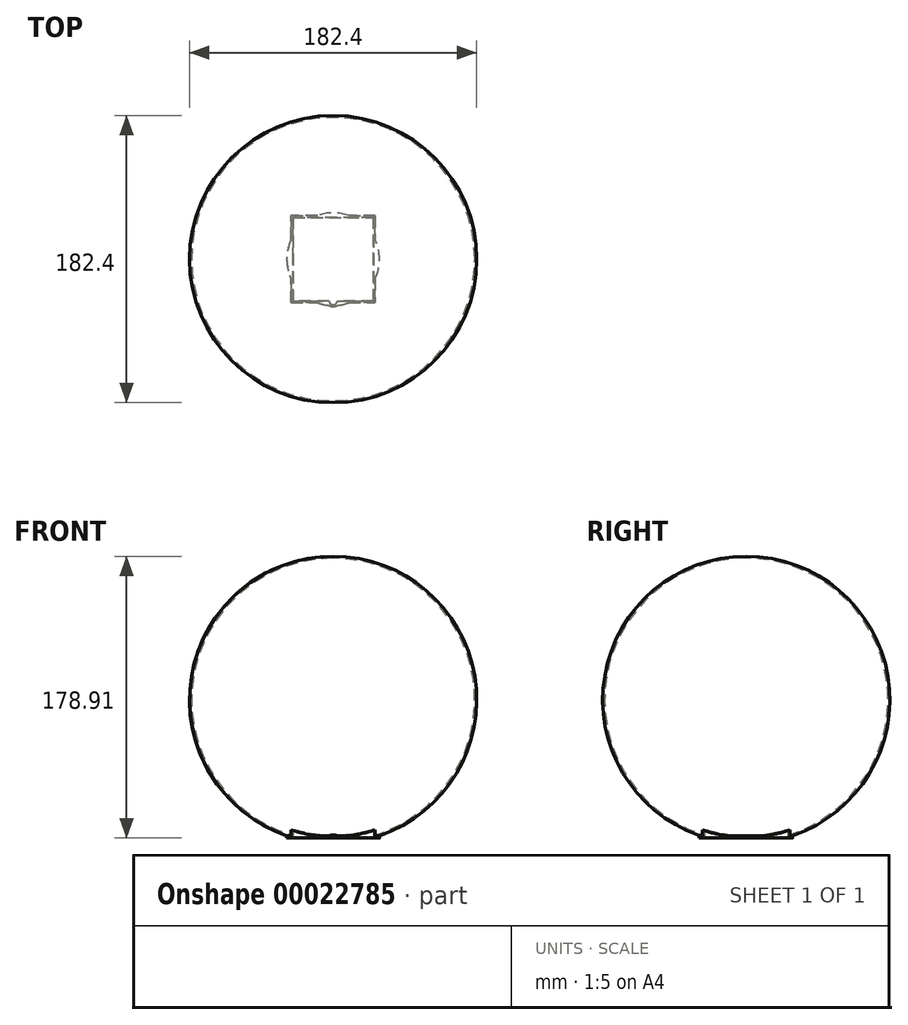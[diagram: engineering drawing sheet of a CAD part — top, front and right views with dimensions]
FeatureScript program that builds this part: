
annotation { "Feature Type Name" : "Feature", "Feature Type Description" : "" }
export const myFeature = defineFeature(function(context is Context, id is Id, definition is map)
    precondition{}
    {
        {
            var Q0;
            Q0=qCreatedBy(makeId("Top.planeOp"),FACE);
            var sketch = newSketch(context, id + "F0", { "sketchPlane" : qUnion([Q0])});
            skLineSegment(sketch, "E0.bottom", {"start": v(-25.5, 26.5) * mm, "end": v(25.5, 26.5) * mm});
            skLineSegment(sketch, "E0.top", {"start": v(-25.5, -26.5) * mm, "end": v(-2.5, -26.5) * mm});
            skLineSegment(sketch, "E0.left", {"start": v(-25.5, 26.5) * mm, "end": v(-25.5, -26.5) * mm});
            skLineSegment(sketch, "E0.right", {"start": v(25.5, 26.5) * mm, "end": v(25.5, -26.5) * mm});
            skPoint(sketch, "E0.middle", {"position": v(0, 0) * mm});
            skArc(sketch, "E1", {"start": v(-2.5, -26.5) * mm, "mid": v(0, -29) * mm, "end": v(2.5, -26.5) * mm});
            skLineSegment(sketch, "E2.trimOffspring", {"start": v(2.5, -26.5) * mm, "end": v(25.5, -26.5) * mm});
            skSolve(sketch);
        }
        {
            var Q0;
            Q0=makeQuery(id+"F0.imprint","IMPRINT",FACE,{"disambiguationData":[TD([[makeQuery(id+"F0.imprint","IMPRINT",EDGE,{"derivedFrom":sQuery(id+"F0.wireOp",EDGE,"E0.bottom")}),-1.0]])]});
            extrude(context, id + "F1", {"entities" : qUnion([Q0]), "depth" : 3 * mm});
        }
        {
            var Q0;
            Q0=qCreatedBy(makeId("Front.planeOp"),FACE);
            var sketch = newSketch(context, id + "F2", { "sketchPlane" : qUnion([Q0])});
            skLineSegment(sketch, "E3", {"start": v(0, 0) * mm, "end": v(0, 176.31) * mm});
            skLineSegment(sketch, "E4.0", {"start": v(-25.5, 0) * mm, "end": v(-2.5, 0) * mm});
            skLineSegment(sketch, "E4.1", {"start": v(-2.5, 0) * mm, "end": v(2.5, 0) * mm});
            skLineSegment(sketch, "E4.2", {"start": v(2.5, 0) * mm, "end": v(25.5, 0) * mm});
            skArc(sketch, "E5", {"start": v(-25.5, 0) * mm, "mid": v(0, 176.31) * mm, "end": v(25.5, 0) * mm});
            skSolve(sketch);
        }
        {
            var Q0;
            {var subQ3=sQuery(id+"F2.wireOp",EDGE,"E3");Q0=makeQuery(id+"F2.imprint","IMPRINT",FACE,{"disambiguationData":[TD([[makeQuery(id+"F2.imprint","IMPRINT",EDGE,{"derivedFrom":subQ3}),1.0]])]});}
            var Q1;
            Q1=sQuery(id+"F2.wireOp",EDGE,"E3");
            revolve(context, id + "F3", {"operationType" : NewBodyOperationType.ADD, "entities" : qUnion([Q0]), "axis" : qUnion([Q1]), "revolveType" : RevolveType.FULL});
        }
        {
            var Q0;
            Q0=makeQuery(id+"F1.opExtrude","CAP_FACE",FACE,{"disambiguationData":[OSD([sQuery(id+"F0.wireOp",EDGE,"E0.bottom"),sQuery(id+"F0.wireOp",EDGE,"E0.top"),sQuery(id+"F0.wireOp",EDGE,"E0.left"),sQuery(id+"F0.wireOp",EDGE,"E0.right")])],"isStart":true});
            shell(context, id + "F4", {"entities" : qUnion([Q0]), "thickness" : 1.2 * mm, "oppositeDirection" : true});
        }
        {
            var Q0;
            Q0=makeQuery(id+"F1.opExtrude","CAP_FACE",FACE,{"disambiguationData":[OSD([sQuery(id+"F0.wireOp",EDGE,"E0.bottom"),sQuery(id+"F0.wireOp",EDGE,"E0.top"),sQuery(id+"F0.wireOp",EDGE,"E0.left"),sQuery(id+"F0.wireOp",EDGE,"E0.right")])],"isStart":true});
            extrude(context, id + "F5", {"entities" : qUnion([Q0]), "operationType" : NewBodyOperationType.ADD, "depth" : 1.4 * mm});
        }
        {
            var Q0;
            {var subQ0=sQuery(id+"F2.wireOp",EDGE,"E5");var subQ1=sQuery(id+"F0.wireOp",EDGE,"E2.trimOffspring");var subQ2=sQuery(id+"F0.wireOp",EDGE,"E1");var subQ3=sQuery(id+"F0.wireOp",EDGE,"E0.right");var subQ4=sQuery(id+"F0.wireOp",EDGE,"E0.left");var subQ5=sQuery(id+"F0.wireOp",EDGE,"E0.top");var subQ6=sQuery(id+"F0.wireOp",EDGE,"E0.bottom");Q0=makeQuery(id+"F4.opShell","OFFSET_EDGE",EDGE,{"disambiguationData":[OSD([subQ6,subQ5,subQ4,subQ3,subQ2,subQ1,subQ0]),TDD([makeQuery(id+"F3.boolean.opBoolean","INTERSECT",EDGE,{"disambiguationData":[OD(0.0)],"derivedFrom":[makeQuery(id+"F1.opExtrude","CAP_FACE",FACE,{"disambiguationData":[OSD([subQ6,subQ5,subQ4,subQ3,subQ2,subQ1])],"isStart":false}),makeQuery(id+"F3.opRevolve","SWEPT_FACE",FACE,{"disambiguationData":[OSD([subQ0])]})]})])]});}
            var Q1;
            {var subQ0=sQuery(id+"F2.wireOp",EDGE,"E5");var subQ1=sQuery(id+"F0.wireOp",EDGE,"E2.trimOffspring");var subQ2=sQuery(id+"F0.wireOp",EDGE,"E1");var subQ3=sQuery(id+"F0.wireOp",EDGE,"E0.right");var subQ4=sQuery(id+"F0.wireOp",EDGE,"E0.left");var subQ5=sQuery(id+"F0.wireOp",EDGE,"E0.top");var subQ6=sQuery(id+"F0.wireOp",EDGE,"E0.bottom");Q1=makeQuery(id+"F4.opShell","OFFSET_EDGE",EDGE,{"disambiguationData":[OSD([subQ6,subQ5,subQ4,subQ3,subQ2,subQ1,subQ0]),TDD([makeQuery(id+"F3.boolean.opBoolean","INTERSECT",EDGE,{"disambiguationData":[OD(1.0)],"derivedFrom":[makeQuery(id+"F1.opExtrude","CAP_FACE",FACE,{"disambiguationData":[OSD([subQ6,subQ5,subQ4,subQ3,subQ2,subQ1])],"isStart":false}),makeQuery(id+"F3.opRevolve","SWEPT_FACE",FACE,{"disambiguationData":[OSD([subQ0])]})]})])]});}
            var Q2;
            {var subQ0=sQuery(id+"F2.wireOp",EDGE,"E5");var subQ1=sQuery(id+"F0.wireOp",EDGE,"E2.trimOffspring");var subQ2=sQuery(id+"F0.wireOp",EDGE,"E1");var subQ3=sQuery(id+"F0.wireOp",EDGE,"E0.right");var subQ4=sQuery(id+"F0.wireOp",EDGE,"E0.left");var subQ5=sQuery(id+"F0.wireOp",EDGE,"E0.top");var subQ6=sQuery(id+"F0.wireOp",EDGE,"E0.bottom");Q2=makeQuery(id+"F4.opShell","OFFSET_EDGE",EDGE,{"disambiguationData":[OSD([subQ6,subQ5,subQ4,subQ3,subQ2,subQ1,subQ0]),TDD([makeQuery(id+"F3.boolean.opBoolean","INTERSECT",EDGE,{"disambiguationData":[OD(3.0)],"derivedFrom":[makeQuery(id+"F1.opExtrude","CAP_FACE",FACE,{"disambiguationData":[OSD([subQ6,subQ5,subQ4,subQ3,subQ2,subQ1])],"isStart":false}),makeQuery(id+"F3.opRevolve","SWEPT_FACE",FACE,{"disambiguationData":[OSD([subQ0])]})]})])]});}
            var Q3;
            {var subQ0=sQuery(id+"F2.wireOp",EDGE,"E5");var subQ1=sQuery(id+"F0.wireOp",EDGE,"E2.trimOffspring");var subQ2=sQuery(id+"F0.wireOp",EDGE,"E1");var subQ3=sQuery(id+"F0.wireOp",EDGE,"E0.right");var subQ4=sQuery(id+"F0.wireOp",EDGE,"E0.left");var subQ5=sQuery(id+"F0.wireOp",EDGE,"E0.top");var subQ6=sQuery(id+"F0.wireOp",EDGE,"E0.bottom");Q3=makeQuery(id+"F4.opShell","OFFSET_EDGE",EDGE,{"disambiguationData":[OSD([subQ6,subQ5,subQ4,subQ3,subQ2,subQ1,subQ0]),TDD([makeQuery(id+"F3.boolean.opBoolean","INTERSECT",EDGE,{"disambiguationData":[OD(2.0)],"derivedFrom":[makeQuery(id+"F1.opExtrude","CAP_FACE",FACE,{"disambiguationData":[OSD([subQ6,subQ5,subQ4,subQ3,subQ2,subQ1])],"isStart":false}),makeQuery(id+"F3.opRevolve","SWEPT_FACE",FACE,{"disambiguationData":[OSD([subQ0])]})]})])]});}
            chamfer(context, id + "F6", {"entities" : qUnion([Q0, Q1, Q2, Q3]), "width" : 0.6 * mm, "tangentPropagation" : true});
        }
    });
